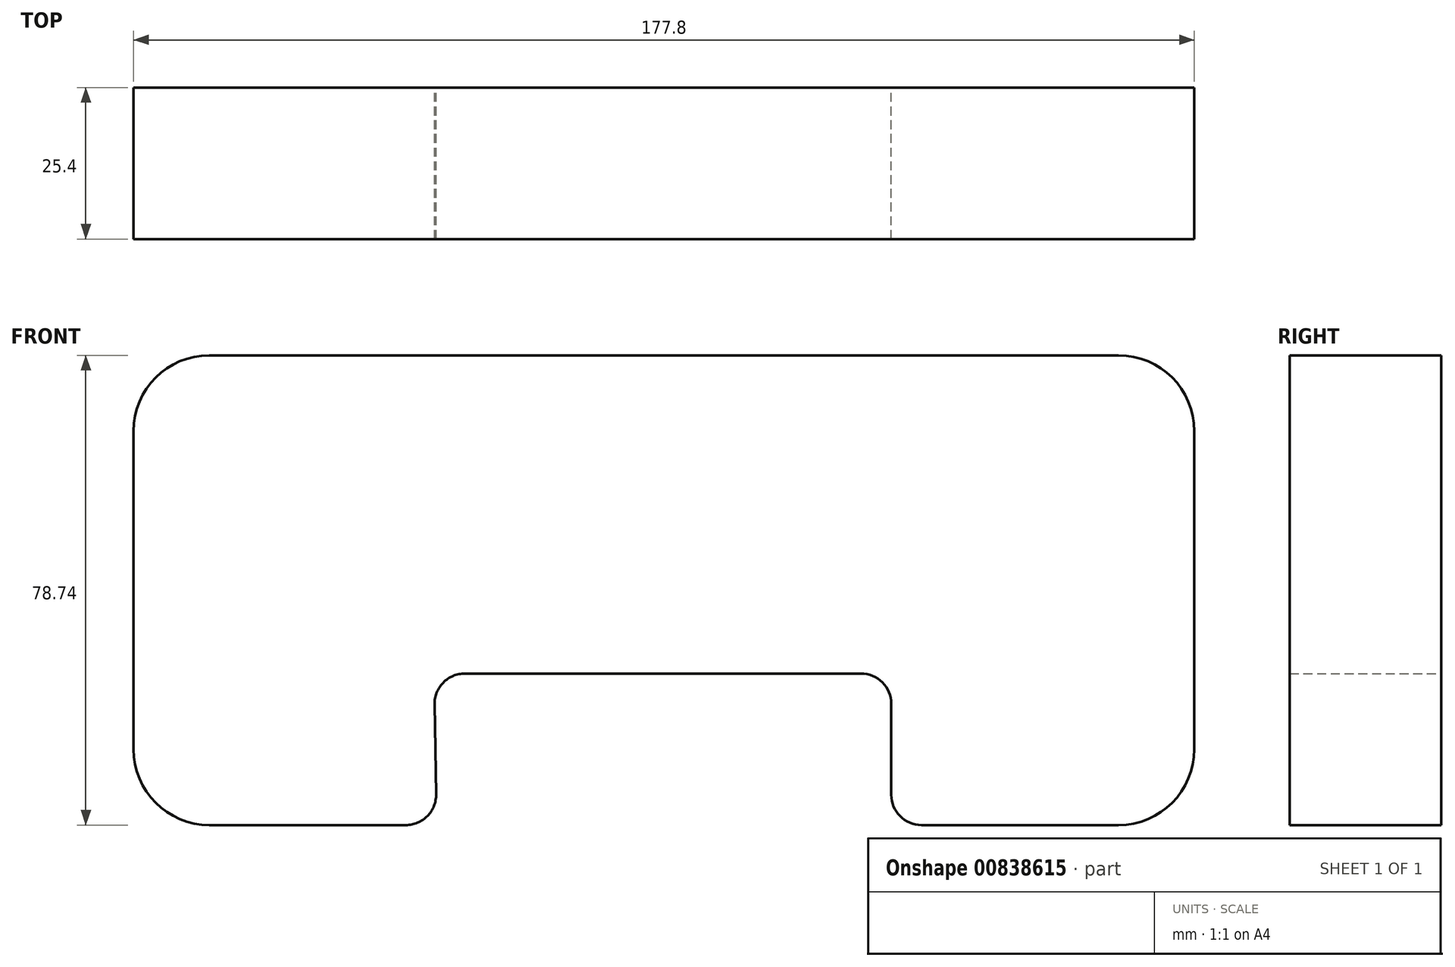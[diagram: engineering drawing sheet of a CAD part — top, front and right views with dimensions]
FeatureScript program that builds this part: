
annotation { "Feature Type Name" : "Feature", "Feature Type Description" : "" }
export const myFeature = defineFeature(function(context is Context, id is Id, definition is map)
    precondition{}
    {
        {
            var Q0;
            Q0=qCreatedBy(makeId("Front.planeOp"),FACE);
            var sketch = newSketch(context, id + "F0", { "sketchPlane" : qUnion([Q0])});
            skLineSegment(sketch, "E0", {"start": v(-68.6, 26.74) * mm, "end": v(83.8, 26.74) * mm});
            skLineSegment(sketch, "E1", {"start": v(96.5, 14.04) * mm, "end": v(96.5, -39.3) * mm});
            skLineSegment(sketch, "E2", {"start": v(-81.3, 14.04) * mm, "end": v(-81.3, -39.3) * mm});
            skLineSegment(sketch, "E3", {"start": v(-68.6, -52) * mm, "end": v(-35.66, -52) * mm});
            skLineSegment(sketch, "E4", {"start": v(83.8, -52) * mm, "end": v(50.79, -52) * mm});
            skLineSegment(sketch, "E5", {"start": v(45.7, -46.92) * mm, "end": v(45.7, -31.69) * mm});
            skLineSegment(sketch, "E6", {"start": v(40.63, -26.6) * mm, "end": v(-25.77, -26.6) * mm});
            skLineSegment(sketch, "E7", {"start": v(-30.85, -31.77) * mm, "end": v(-30.58, -46.83) * mm});
            skPoint(sketch, "E8.visualSharp", {"position": v(-81.3, 26.74) * mm});
            skArc(sketch, "E8.filletArc", {"start": v(-68.6, 26.74) * mm, "mid": v(-77.57, 23.02) * mm, "end": v(-81.3, 14.04) * mm});
            skPoint(sketch, "E9.visualSharp", {"position": v(96.5, 26.74) * mm});
            skArc(sketch, "E9.filletArc", {"start": v(96.5, 14.04) * mm, "mid": v(92.79, 23.02) * mm, "end": v(83.8, 26.74) * mm});
            skPoint(sketch, "E10.visualSharp", {"position": v(96.5, -52) * mm});
            skArc(sketch, "E10.filletArc", {"start": v(83.8, -52) * mm, "mid": v(92.79, -48.28) * mm, "end": v(96.5, -39.3) * mm});
            skPoint(sketch, "E11.visualSharp", {"position": v(-81.3, -52) * mm});
            skArc(sketch, "E11.filletArc", {"start": v(-81.3, -39.3) * mm, "mid": v(-77.57, -48.28) * mm, "end": v(-68.6, -52) * mm});
            skPoint(sketch, "E12.visualSharp", {"position": v(-30.5, -52) * mm});
            skArc(sketch, "E12.filletArc", {"start": v(-35.66, -52) * mm, "mid": v(-32.04, -50.48) * mm, "end": v(-30.58, -46.83) * mm});
            skPoint(sketch, "E13.visualSharp", {"position": v(-30.94, -26.6) * mm});
            skArc(sketch, "E13.filletArc", {"start": v(-25.77, -26.6) * mm, "mid": v(-29.39, -28.13) * mm, "end": v(-30.85, -31.77) * mm});
            skPoint(sketch, "E14.visualSharp", {"position": v(45.7, -26.6) * mm});
            skArc(sketch, "E14.filletArc", {"start": v(45.7, -31.69) * mm, "mid": v(44.22, -28.1) * mm, "end": v(40.63, -26.6) * mm});
            skPoint(sketch, "E15.visualSharp", {"position": v(45.7, -52) * mm});
            skArc(sketch, "E15.filletArc", {"start": v(45.7, -46.92) * mm, "mid": v(47.2, -50.51) * mm, "end": v(50.79, -52) * mm});
            skSolve(sketch);
        }
        {
            var Q0;
            Q0 = qSketchRegion(id + "F0", true);
            extrude(context, id + "F1", {"entities" : qUnion([Q0]), "depth" : 25.4 * mm, "offsetDistance" : 25.4 * mm});
        }
    });
